# Revit family: LAMP_FIL 50 G2 OPAL SUSPENDED DALI
name_source: partatom
category: Luminarias
revit_build: Autodesk Revit 2015 (Build: 20140606_1530(x64)
units: mm (PartAtom-declared; Revit-internal decimal feet)

## types (16) — shared parameters
CRI = 80
Cambio de temperatura de color de luz atenuada = <Ninguno>
Fabricante = LAMP
Filtro de color = 16777215
Gear = Adjustable DALI
IEE = A++
IFC Clasificación = Light Fixture
Installation instructions = https://www.lamp.es
Insulation class = I
Luminaire type = Indoor - Modular Systems
Lámpara = MID-POWER LED
MacAdam = 3
Manufacturer URL = http://www.lamp.es
Manufacturer country = Spain
Manufacturer name = LAMP
Material Difusor = LAMP_PC Difusor Opal Fil
Power Supply = 220-240V 50-60Hz
Product URL = https://www.lamp.es
Product datasheet = https://www.lamp.es
Protection rating = IP42, IK07
Type = MID POWER TRIDONIC
Ángulo de inclinación = 90,00°

## per-type parameters (varying)
| type | Archivo de red fotométrica | Comentarios de tipo | Descripción | Dimensions | Efficacy | Finish | LED Lifetime | Largo | Last update | Longitud de línea de emisión | Material Perfil | Material codo | Model explanation | Modelo | Plum | Power | Product code | UniClass 1.4 Code | UniClass 2.0 Code | Weight |
| 1137MM 3000LM 3000K WHITE | 14741400.IES | Availability of switching between accessories through visibility parameters when placed in a project. | FIL 50 G2 OPAL SUS 3000 WW DALI WH. | 1137x50x67mm | 89 lm/W | Matt white | 50000 L80 B10 | 1137 mm  [stored 3.73031 ft] | 07/07/2020 | 1137 mm  [stored 3.73031 ft] | LAMP_Aluminio Perfil Fil BL | LAMP_Aluminio Perfil Fil BL | Availability of switching between accessories through visibility parameters when placed in a project. | F52SF120MOOP830DW | 21 W | 19 W | F52SF120MOOP830DW | F52SF120MOOP830DW | F52SF120MOOP830DW | 2,11 kg |
| 1137MM 3000LM 3000K GREY | 14741403.IES | Availability of switching between accessories through visibility parameters when placed in a project.
Availability of switching between accessories through visibility parameters when placed in a project. | FIL 50 G2 OPAL SUS 3000 WW DALI GR. | 1137x50x67mm | 89 lm/W | Gloss grey | 50000 L80 B10 | 1137 mm  [stored 3.73031 ft] | 07/07/2020 | 1137 mm  [stored 3.73031 ft] | LAMP_Aluminio Perfil Fil GR | LAMP_Aluminio Perfil Fil GR | Availability of switching between accessories through visibility parameters when placed in a project.
Availability of switching between accessories through visibility parameters when placed in a project. | F52SF120MOOP830DG | 21 W | 19 W | F52SF120MOOP830DG | F52SF120MOOP830DG | F52SF120MOOP830DG | 2,11 kg |
| 1137MM 3000LM 4000K WHITE | 14740400.IES | Availability of switching between accessories through visibility parameters when placed in a project. | FIL 50 G2 OPAL SUS 3000 NW DALI WH. | 1137x50x67mm | 94 lm/W | Matt white | 50000 L80 B10 | 1137 mm  [stored 3.73031 ft] | 07/07/2020 | 1137 mm  [stored 3.73031 ft] | LAMP_Aluminio Perfil Fil BL | LAMP_Aluminio Perfil Fil BL | Availability of switching between accessories through visibility parameters when placed in a project. | F52SF120MOOP840DW | 21 W | 19 W | F52SF120MOOP840DW | F52SF120MOOP840DW | F52SF120MOOP840DW | 2,11 kg |
| 1137MM 3000LM 4000K GREY | 14740403.IES | Availability of switching between accessories through visibility parameters when placed in a project. | FIL 50 G2 OPAL SUS 3000 NW DALI GR. | 1137x50x67mm | 94 lm/W | Gloss grey | 50000 L80 B10 | 1137 mm  [stored 3.73031 ft] | 07/07/2020 | 1137 mm  [stored 3.73031 ft] | LAMP_Aluminio Perfil Fil GR | LAMP_Aluminio Perfil Fil GR | Availability of switching between accessories through visibility parameters when placed in a project. | F52SF120MOOP840DG | 21 W | 19 W | F52SF120MOOP840DG | F52SF120MOOP840DG | F52SF120MOOP840DG | 2,11 kg |
| 1137MM 6000LM 3000K WHITE | 14741420.IES | Availability of switching between accessories through visibility parameters when placed in a project. | FIL 50 G2 OPAL SUS 6000 WW DALI WH. | 1137x50x67mm | 88 lm/W | Matt white | 50000 L70 B10 | 1137 mm  [stored 3.73031 ft] | 07/07/2020
07/07/2020 | 1137 mm  [stored 3.73031 ft] | LAMP_Aluminio Perfil Fil BL | LAMP_Aluminio Perfil Fil BL | Availability of switching between accessories through visibility parameters when placed in a project. | F52SF120HOOP830DW | 41 W | 37 W | F52SF120HOOP830DW | F52SF120HOOP830DW | F52SF120HOOP830DW | 2,11 kg |
| 1137MM 6000LM 3000K GREY | 14741423.IES | Availability of switching between accessories through visibility parameters when placed in a project. | FIL 50 G2 OPAL SUS 6000 WW DALI GR. | 1137x50x67mm | 88 lm/W | Gloss grey | 50000 L70 B10 | 1137 mm  [stored 3.73031 ft] | 07/07/2020 | 1137 mm  [stored 3.73031 ft] | LAMP_Aluminio Perfil Fil GR | LAMP_Aluminio Perfil Fil GR | Availability of switching between accessories through visibility parameters when placed in a project. | F52SF120HOOP830DG | 41 W | 37 W | F52SF120HOOP830DG | F52SF120HOOP830DG | F52SF120HOOP830DG | 2,11 kg |
| 1137MM 6000LM 4000K WHITE | 14740423.IES | Availability of switching between accessories through visibility parameters when placed in a project. | FIL 50 G2 OPAL SUS 6000 NW DALI GR. | 1137x50x67mm | 93 lm/W | Gloss grey | 50000 L70 B10 | 1137 mm  [stored 3.73031 ft] | 07/07/2020 | 1137 mm  [stored 3.73031 ft] | LAMP_Aluminio Perfil Fil BL | LAMP_Aluminio Perfil Fil BL | Availability of switching between accessories through visibility parameters when placed in a project. | F52SF120HOOP840DW | 41 W | 37 W | F52SF120HOOP840DW | F52SF120HOOP840DW | F52SF120HOOP840DW | 2,11 kg |
| 1137MM 6000LM 4000K GREY | 14740420.IES | Availability of switching between accessories through visibility parameters when placed in a project. | FIL 50 G2 OPAL SUS 6000 NW DALI WH. | 1137x50x67mm | 93 lm/W | Matt white | 50000 L70 B10 | 1137 mm  [stored 3.73031 ft] | 07/07/2020 | 1137 mm  [stored 3.73031 ft] | LAMP_Aluminio Perfil Fil GR | LAMP_Aluminio Perfil Fil GR | Availability of switching between accessories through visibility parameters when placed in a project. | F52SF120HOOP840DG | 41 W | 37 W | F52SF120HOOP840DG | F52SF120HOOP840DG | F52SF120HOOP840DG | 2,11 kg |
| 1700MM 4600LM 3000K WHITE | 14741410.IES | Availability of switching between accessories through visibility parameters when placed in a project. | FIL 50 G2 OPAL SUS 4600 WW DALI WH. | 1700x50x67mm | 89 lm/W | Matt white | 50000 L80 B10 | 1700 mm  [stored 5.57743 ft] | 07/07/2020 | 1700 mm  [stored 5.57743 ft] | LAMP_Aluminio Perfil Fil BL | LAMP_Aluminio Perfil Fil BL | Availability of switching between accessories through visibility parameters when placed in a project. | F52SF170MOOP830DW | 32 W | 28 W | F52SF170MOOP830DW | F52SF170MOOP830DW | F52SF170MOOP830DW | 2,77 kg |
| 1700MM 4600LM 3000K GREY | 14741413.IES | Availability of switching between accessories through visibility parameters when placed in a project. | FIL 50 G2 OPAL SUS 4600 WW DALI GR. | 1700x50x67mm | 89 lm/W | Gloss grey | 50000 L80 B10 | 1700 mm  [stored 5.57743 ft] | 07/07/2020 | 1700 mm  [stored 5.57743 ft] | LAMP_Aluminio Perfil Fil GR | LAMP_Aluminio Perfil Fil GR | Availability of switching between accessories through visibility parameters when placed in a project. | F52SF170MOOP830DG | 32 W | 28 W | F52SF170MOOP830DG | F52SF170MOOP830DG | F52SF170MOOP830DG | 2,77 kg |
| 1700MM 4600LM 4000K WHITE | 14740410.IES | Availability of switching between accessories through visibility parameters when placed in a project. | FIL 50 G2 OPAL SUS 4600 NW DALI WH. | 1700x50x67mm | 93 lm/W | Matt white | 50000 L80 B10 | 1700 mm  [stored 5.57743 ft] | 07/07/2020 | 1700 mm  [stored 5.57743 ft] | LAMP_Aluminio Perfil Fil BL | LAMP_Aluminio Perfil Fil BL | Availability of switching between accessories through visibility parameters when placed in a project. | F52SF170MOOP840DW | 32 W | 28 W | F52SF170MOOP840DW | F52SF170MOOP840DW | F52SF170MOOP840DW | 2,77 kg |
| 1700MM 4600LM 4000K GREY | 14740413.IES | Availability of switching between accessories through visibility parameters when placed in a project. | FIL 50 G2 OPAL SUS 4600 NW DALI GR. | 1700x50x67mm | 93 lm/W | Gloss grey | 50000 L80 B10 | 1700 mm  [stored 5.57743 ft] | 07/07/2020 | 1700 mm  [stored 5.57743 ft] | LAMP_Aluminio Perfil Fil GR | LAMP_Aluminio Perfil Fil GR | Availability of switching between accessories through visibility parameters when placed in a project. | F52SF170MOOP840DG | 32 W | 28 W | F52SF170MOOP840DG | F52SF170MOOP840DG | F52SF170MOOP840DG | 2,77 kg |
| 1700MM 9200LM 3000K WHITE | 14741430.IES | Availability of switching between accessories through visibility parameters when placed in a project. | FIL 50 G2 OPAL SUS 9200 WW DALI WH. | 1700x50x67mm | 89 lm/W | Matt white | 50000 L70 B10 | 1700 mm  [stored 5.57743 ft] | 07/07/2020 | 1700 mm  [stored 5.57743 ft] | LAMP_Aluminio Perfil Fil BL | LAMP_Aluminio Perfil Fil BL | Availability of switching between accessories through visibility parameters when placed in a project. | F52SF170HOOP830DW | 60 W | 55 W | F52SF170HOOP830DW | F52SF170HOOP830DW | F52SF170HOOP830DW | 2,77 kg |
| 1700MM 9200LM 3000K GREY | 14741433.IES | Availability of switching between accessories through visibility parameters when placed in a project. | FIL 50 G2 OPAL SUS 9200 WW DALI GR. | 1700x50x67mm | 89 lm/W | Gloss grey | 50000 L70 B10 | 1700 mm  [stored 5.57743 ft] | 07/07/2020 | 1700 mm  [stored 5.57743 ft] | LAMP_Aluminio Perfil Fil GR | LAMP_Aluminio Perfil Fil GR | Availability of switching between accessories through visibility parameters when placed in a project. | F52SF170HOOP830DG | 60 W | 55 W | F52SF170HOOP830DG | F52SF170HOOP830DG | F52SF170HOOP830DG | 2,77 kg |
| 1700MM 9200LM 4000K WHITE | 14740430.IES | Availability of switching between accessories through visibility parameters when placed in a project. | FIL 50 G2 OPAL SUS 9200 NW DALI WH. | 1700x50x67mm | 93 lm/W | Matt white | 50000 L70 B10 | 1700 mm  [stored 5.57743 ft] | 07/07/2020 | 1700 mm  [stored 5.57743 ft] | LAMP_Aluminio Perfil Fil BL | LAMP_Aluminio Perfil Fil BL | Availability of switching between accessories through visibility parameters when placed in a project. | F52SF170HOOP840DW | 60 W | 55 W | F52SF170HOOP840DW | F52SF170HOOP840DW | F52SF170HOOP840DW | 2,77 kg |
| 1700MM 9200LM 4000K GREY | 14740433.IES | Availability of switching between accessories through visibility parameters when placed in a project. | FIL 50 G2 OPAL SUS 9200 NW DALI GR. | 1700x50x67mm | 93 lm/W | Gloss grey | 50000 L70 B10 | 1700 mm  [stored 5.57743 ft] | 07/07/2020 | 1700 mm  [stored 5.57743 ft] | LAMP_Aluminio Perfil Fil GR | LAMP_Aluminio Perfil Fil GR | Availability of switching between accessories through visibility parameters when placed in a project. | F52SF170HOOP840DG | 60 W | 55 W | F52SF170HOOP840DG | F52SF170HOOP840DG | F52SF170HOOP840DG | 2,77 kg |

note: [stored X ft] marks values corroborated as IEEE doubles in the binary element streams (Revit-internal decimal feet)

## geometry (parser evidence)
native form markers: Blend x3
no freeform markers — native parametric forms only
